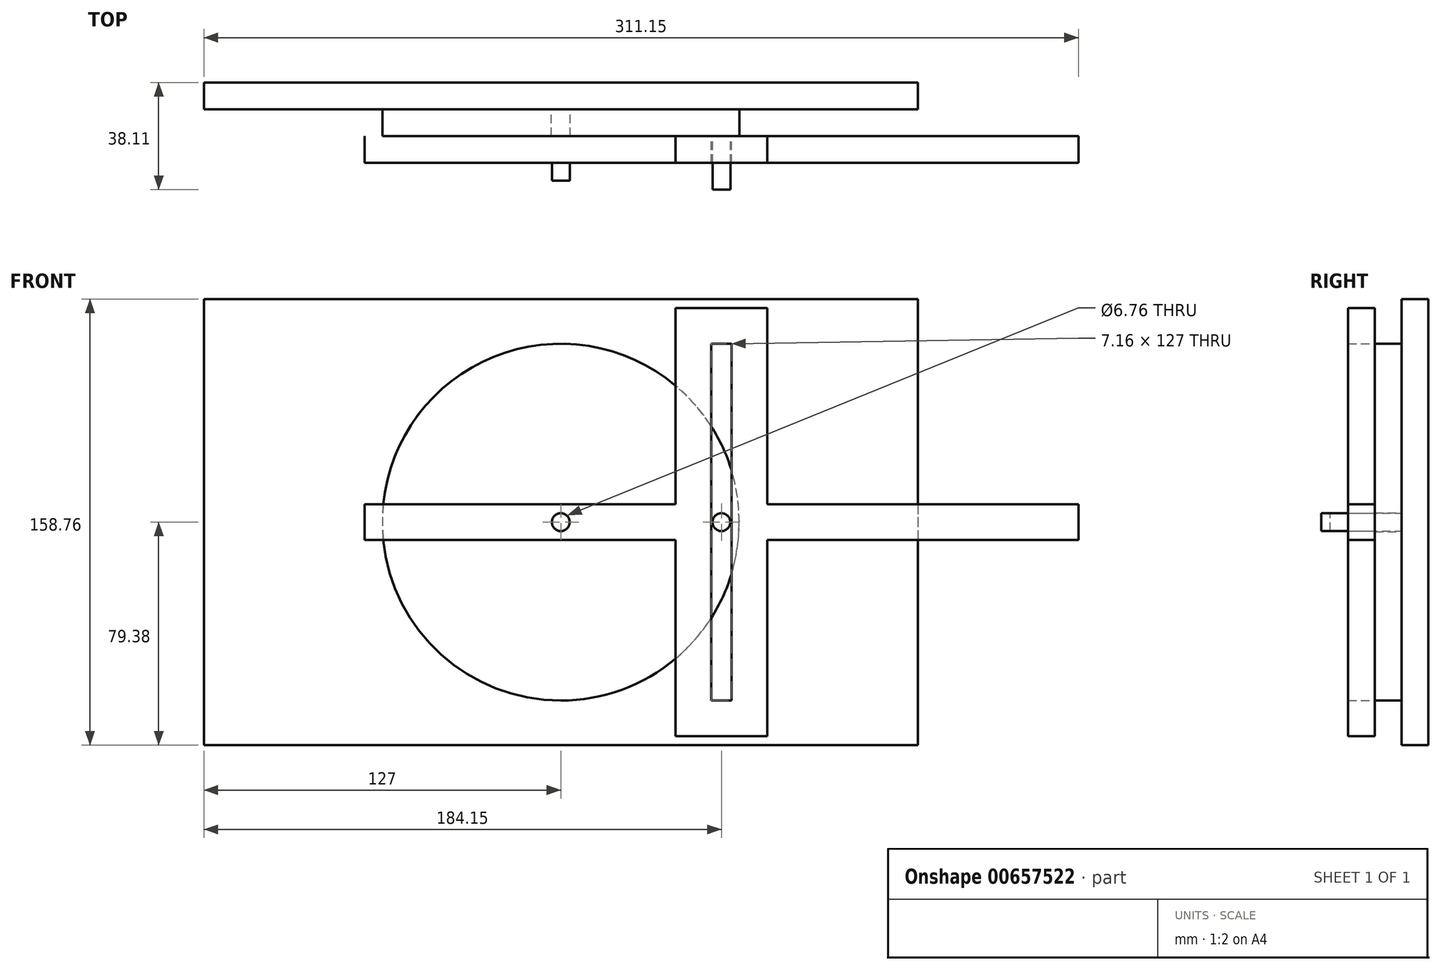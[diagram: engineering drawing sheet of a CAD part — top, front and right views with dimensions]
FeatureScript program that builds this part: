
annotation { "Feature Type Name" : "Feature", "Feature Type Description" : "" }
export const myFeature = defineFeature(function(context is Context, id is Id, definition is map)
    precondition{}
    {
        {
            assignVariable(context, id + "F0", {"name" : "mat", "anyValue" : 9.52 * mm});
        }
        {
            var Q0;
            Q0=qCreatedBy(makeId("Front.planeOp"),FACE);
            var sketch = newSketch(context, id + "F1", { "sketchPlane" : qUnion([Q0])});
            skCircle(sketch, "E0", {"center": v(0, 0) * mm, "radius": 3.38 * mm});
            skCircle(sketch, "E1", {"center": v(0, 0) * mm, "radius": 63.5 * mm});
            skSolve(sketch);
        }
        {
            var Q0;
            Q0=makeQuery(id+"F1.imprint","IMPRINT",FACE,{"disambiguationData":[TD([[makeQuery(id+"F1.imprint","IMPRINT",EDGE,{"derivedFrom":sQuery(id+"F1.wireOp",EDGE,"E0")}),-1.0]])]});
            extrude(context, id + "F2", {"entities" : qUnion([Q0]), "depth" : getVariable(context, 'mat'), "offsetDistance" : 25.4 * mm});
        }
        {
            var Q0;
            Q0=makeQuery(id+"F2.opExtrude","CAP_FACE",FACE,{"disambiguationData":[OSD([sQuery(id+"F1.wireOp",EDGE,"E0"),sQuery(id+"F1.wireOp",EDGE,"E1")])],"isStart":false});
            var sketch = newSketch(context, id + "F3", { "sketchPlane" : qUnion([Q0])});
            skCircle(sketch, "E2", {"center": v(57.15, 0) * mm, "radius": 3.18 * mm});
            skLineSegment(sketch, "E3.bottom", {"start": v(53.57, 63.5) * mm, "end": v(60.73, 63.5) * mm});
            skLineSegment(sketch, "E3.top", {"start": v(53.57, -63.5) * mm, "end": v(60.73, -63.5) * mm});
            skLineSegment(sketch, "E3.left", {"start": v(53.57, 63.5) * mm, "end": v(53.57, -63.5) * mm});
            skLineSegment(sketch, "E3.right", {"start": v(60.73, 63.5) * mm, "end": v(60.73, -63.5) * mm});
            skLineSegment(sketch, "E4", {"start": v(57.15, 63.5) * mm, "end": v(57.15, -63.5) * mm, "construction": true});
            skLineSegment(sketch, "E5.bottom", {"start": v(-69.85, 6.35) * mm, "end": v(184.15, 6.35) * mm});
            skLineSegment(sketch, "E5.top", {"start": v(-69.85, -6.35) * mm, "end": v(184.15, -6.35) * mm});
            skLineSegment(sketch, "E5.left", {"start": v(-69.85, 6.35) * mm, "end": v(-69.85, -6.35) * mm});
            skLineSegment(sketch, "E5.right", {"start": v(184.15, 6.35) * mm, "end": v(184.15, -6.35) * mm});
            skLineSegment(sketch, "E6.bottom", {"start": v(73.42, -76.2) * mm, "end": v(40.88, -76.2) * mm});
            skLineSegment(sketch, "E6.top", {"start": v(73.42, 76.2) * mm, "end": v(40.88, 76.2) * mm});
            skLineSegment(sketch, "E6.left", {"start": v(73.42, -76.2) * mm, "end": v(73.42, 76.2) * mm});
            skLineSegment(sketch, "E6.right", {"start": v(40.88, -76.2) * mm, "end": v(40.88, 76.2) * mm});
            skSolve(sketch);
        }
        {
            var Q0;
            Q0=makeQuery(id+"F3.imprint","IMPRINT",FACE,{"disambiguationData":[TD([[makeQuery(id+"F3.imprint","IMPRINT",EDGE,{"derivedFrom":sQuery(id+"F3.wireOp",EDGE,"E2")}),1.0]])]});
            extrude(context, id + "F4", {"entities" : qUnion([Q0]), "operationType" : NewBodyOperationType.ADD, "depth" : getVariable(context, 'mat') * 2, "offsetDistance" : 25.4 * mm});
        }
        {
            var Q0;
            Q0=qSketchRegion(id+"F3",true);
            extrude(context, id + "F5", {"entities" : qUnion([Q0]), "depth" : getVariable(context, 'mat'), "offsetDistance" : 25.4 * mm});
        }
        {
            var Q0;
            Q0=makeQuery(id+"F2.opExtrude","CAP_FACE",FACE,{"disambiguationData":[OSD([sQuery(id+"F1.wireOp",EDGE,"E0"),sQuery(id+"F1.wireOp",EDGE,"E1")])],"isStart":true});
            var sketch = newSketch(context, id + "F6", { "sketchPlane" : qUnion([Q0])});
            skLineSegment(sketch, "E7.bottom", {"start": v(-127, 79.38) * mm, "end": v(127, 79.38) * mm});
            skLineSegment(sketch, "E7.top", {"start": v(-127, -79.38) * mm, "end": v(127, -79.38) * mm});
            skLineSegment(sketch, "E7.left", {"start": v(-127, 79.38) * mm, "end": v(-127, -79.38) * mm});
            skLineSegment(sketch, "E7.right", {"start": v(127, 79.38) * mm, "end": v(127, -79.38) * mm});
            skPoint(sketch, "E7.middle", {"position": v(0, 0) * mm});
            skSolve(sketch);
        }
        {
            var Q0;
            Q0=makeQuery(id+"F6.imprint","IMPRINT",FACE,{"disambiguationData":[TD([[makeQuery(id+"F6.imprint","IMPRINT",EDGE,{"derivedFrom":sQuery(id+"F6.wireOp",EDGE,"E7.bottom")}),-1.0]])]});
            var Q1;
            Q1=makeQuery(id+"F6.imprint","IMPRINT",FACE,{"disambiguationData":[TD([[makeQuery(id+"F6.imprint","IMPRINT",EDGE,{"derivedFrom":makeQuery(id+"F2.opExtrude","CAP_EDGE",EDGE,{"disambiguationData":[OSD([sQuery(id+"F1.wireOp",EDGE,"E0")])],"isStart":true})}),1.0]])]});
            var Q2;
            Q2=makeQuery(id+"F6.imprint","IMPRINT",FACE,{"disambiguationData":[TD([[makeQuery(id+"F6.imprint","IMPRINT",EDGE,{"derivedFrom":makeQuery(id+"F2.opExtrude","CAP_EDGE",EDGE,{"disambiguationData":[OSD([sQuery(id+"F1.wireOp",EDGE,"E0")])],"isStart":true})}),-1.0]])]});
            extrude(context, id + "F7", {"entities" : qUnion([Q0, Q1, Q2]), "depth" : getVariable(context, 'mat'), "offsetDistance" : 25.4 * mm});
        }
        {
            var Q0;
            Q0=makeQuery(id+"F7.opExtrude","CAP_FACE",FACE,{"disambiguationData":[OSD([sQuery(id+"F6.wireOp",EDGE,"E7.bottom"),sQuery(id+"F6.wireOp",EDGE,"E7.top"),sQuery(id+"F6.wireOp",EDGE,"E7.left"),sQuery(id+"F6.wireOp",EDGE,"E7.right")])],"isStart":true});
            var sketch = newSketch(context, id + "F8", { "sketchPlane" : qUnion([Q0])});
            skCircle(sketch, "E8", {"center": v(0, 0) * mm, "radius": 3.18 * mm});
            skSolve(sketch);
        }
        {
            var Q0;
            Q0=makeQuery(id+"F8.imprint","IMPRINT",FACE,{"disambiguationData":[TD([[makeQuery(id+"F8.imprint","IMPRINT",EDGE,{"derivedFrom":sQuery(id+"F8.wireOp",EDGE,"E8")}),1.0]])]});
            extrude(context, id + "F9", {"entities" : qUnion([Q0]), "depth" : 25.4 * mm, "offsetDistance" : 25.4 * mm});
        }
    });
